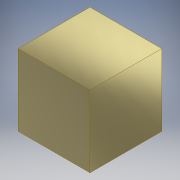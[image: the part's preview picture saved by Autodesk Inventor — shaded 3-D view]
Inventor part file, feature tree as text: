
AUTODESK INVENTOR PART (.ipt)
format: ipt  version: 2018 (Build 220112000, 112)  size: 94,720 bytes
history: native  units: mm
features: extrude x1, sketch x1
ambient origin geometry x8: Origin, YZ Plane, XZ Plane, XY Plane, X Axis, Y Axis, Z Axis, Center Point
bodies: Solid1 (feature_tree)
feature tree (2):
  extrude  "Extrusion1"  Depth=100.0mm
  sketch  "Sketch1"  dims[d0=100.0mm d1=100.0mm d2=100.0mm d3=0.0mm]
